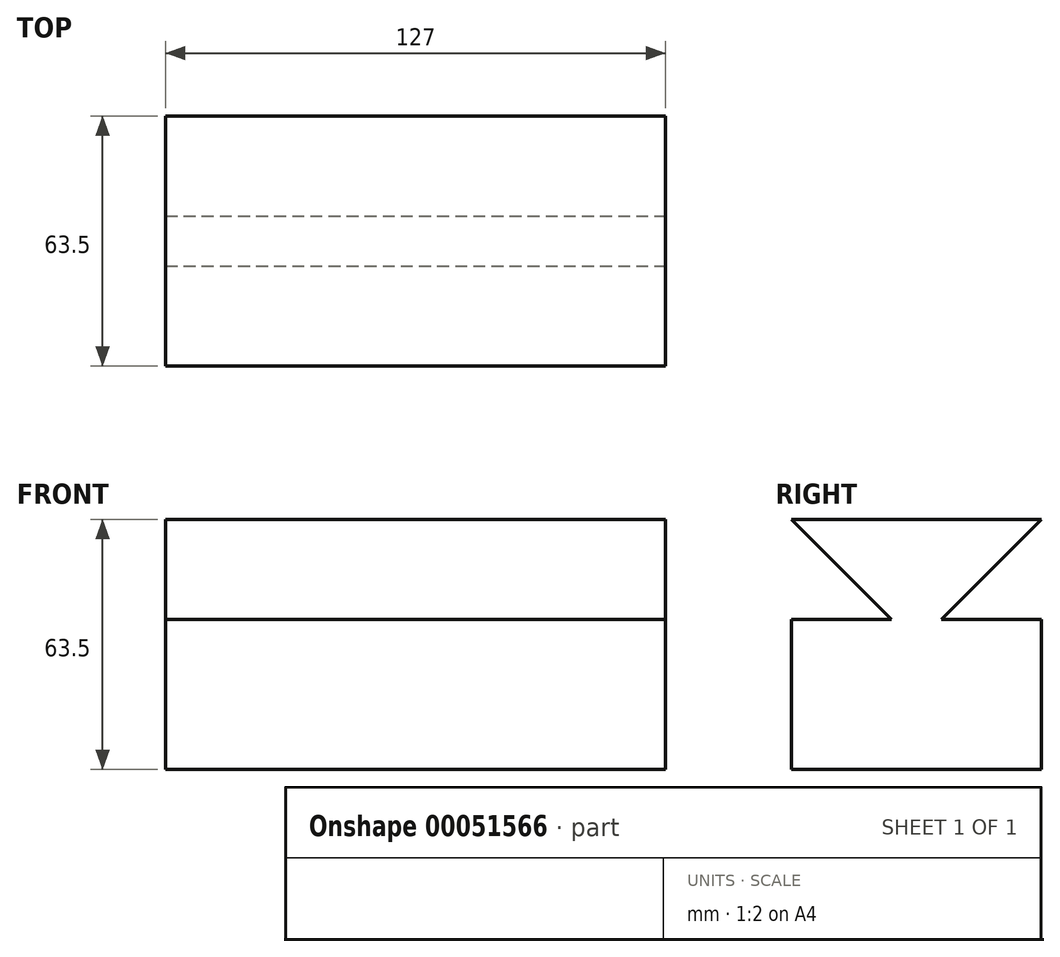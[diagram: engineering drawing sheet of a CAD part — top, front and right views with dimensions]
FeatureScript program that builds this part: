
annotation { "Feature Type Name" : "Feature", "Feature Type Description" : "" }
export const myFeature = defineFeature(function(context is Context, id is Id, definition is map)
    precondition{}
    {
        {
            var Q0;
            Q0=qCreatedBy(makeId("Right.planeOp"),FACE);
            var sketch = newSketch(context, id + "F0", { "sketchPlane" : qUnion([Q0])});
            skLineSegment(sketch, "E0.bottom", {"start": v(-29.76, 30.26) * mm, "end": v(33.74, 30.26) * mm});
            skLineSegment(sketch, "E0.top", {"start": v(-29.76, -33.24) * mm, "end": v(33.74, -33.24) * mm});
            skLineSegment(sketch, "E0.left", {"start": v(-29.76, 30.26) * mm, "end": v(-29.76, -33.24) * mm});
            skLineSegment(sketch, "E0.right", {"start": v(33.74, 30.26) * mm, "end": v(33.74, -33.24) * mm});
            skSolve(sketch);
        }
        {
            var Q0;
            Q0 = qSketchRegion(id + "F0", true);
            extrude(context, id + "F1", {"entities" : qUnion([Q0]), "depth" : 127 * mm});
        }
        {
            var Q0;
            Q0=makeQuery(id+"F1.opExtrude","CAP_FACE",FACE,{"disambiguationData":[OSD([sQuery(id+"F0.wireOp",EDGE,"E0.bottom"),sQuery(id+"F0.wireOp",EDGE,"E0.top"),sQuery(id+"F0.wireOp",EDGE,"E0.left"),sQuery(id+"F0.wireOp",EDGE,"E0.right")])],"isStart":false});
            var sketch = newSketch(context, id + "F2", { "sketchPlane" : qUnion([Q0])});
            skLineSegment(sketch, "E1", {"start": v(-29.76, 4.86) * mm, "end": v(-4.36, 4.86) * mm});
            skLineSegment(sketch, "E2", {"start": v(-29.76, 30.26) * mm, "end": v(-4.36, 4.86) * mm});
            skLineSegment(sketch, "E3", {"start": v(33.74, 30.26) * mm, "end": v(8.34, 4.86) * mm});
            skLineSegment(sketch, "E4", {"start": v(33.74, 30.26) * mm, "end": v(33.74, 4.86) * mm});
            skLineSegment(sketch, "E5", {"start": v(-29.76, 30.26) * mm, "end": v(-29.76, 4.86) * mm});
            skLineSegment(sketch, "E6.trimOffspring", {"start": v(8.34, 4.86) * mm, "end": v(33.74, 4.86) * mm});
            skSolve(sketch);
        }
        {
            var Q0;
            Q0 = qSketchRegion(id + "F2", true);
            extrude(context, id + "F3", {"entities" : qUnion([Q0]), "operationType" : NewBodyOperationType.REMOVE, "endBound" : BoundingType.THROUGH_ALL, "oppositeDirection" : true, "depth" : 25.4 * mm});
        }
    });
